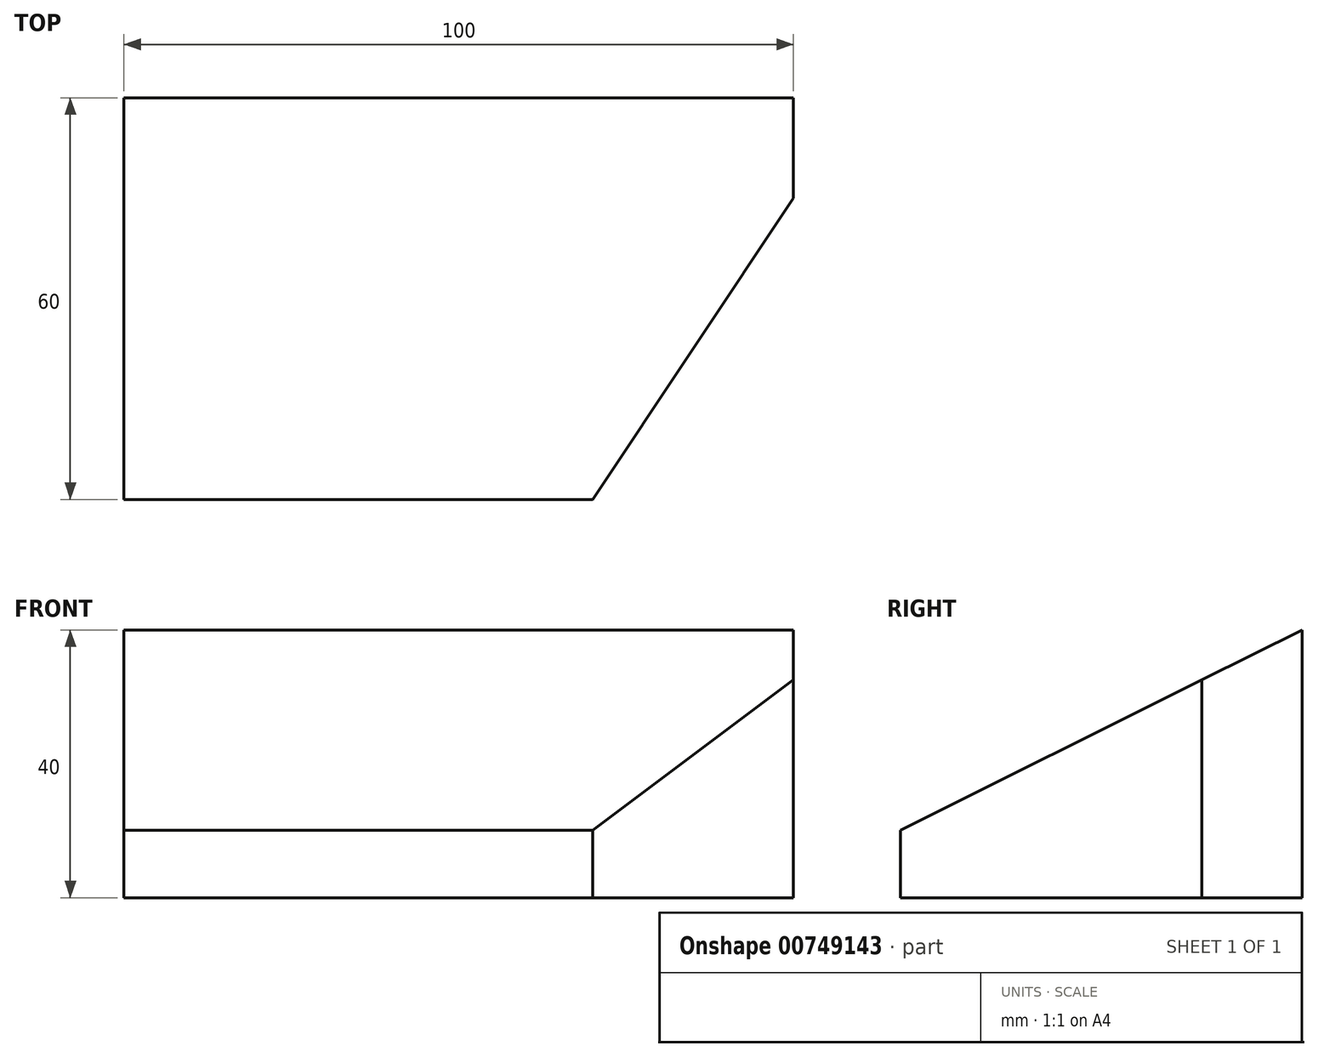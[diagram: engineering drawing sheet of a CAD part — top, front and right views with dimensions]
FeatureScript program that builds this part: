
annotation { "Feature Type Name" : "Feature", "Feature Type Description" : "" }
export const myFeature = defineFeature(function(context is Context, id is Id, definition is map)
    precondition{}
    {
        {
            var Q0;
            Q0=qCreatedBy(makeId("Top.planeOp"),FACE);
            var sketch = newSketch(context, id + "F0", { "sketchPlane" : qUnion([Q0])});
            skLineSegment(sketch, "E0", {"start": v(0, 0) * mm, "end": v(0, 60) * mm});
            skLineSegment(sketch, "E1", {"start": v(0, 60) * mm, "end": v(100, 60) * mm});
            skLineSegment(sketch, "E2", {"start": v(100, 60) * mm, "end": v(100, 45) * mm});
            skLineSegment(sketch, "E3", {"start": v(100, 45) * mm, "end": v(70, 0) * mm});
            skLineSegment(sketch, "E4", {"start": v(70, 0) * mm, "end": v(0, 0) * mm});
            skSolve(sketch);
        }
        {
            var Q0;
            Q0=makeQuery(id+"F0.imprint","IMPRINT",FACE,{"disambiguationData":[TD([[makeQuery(id+"F0.imprint","IMPRINT",EDGE,{"derivedFrom":sQuery(id+"F0.wireOp",EDGE,"E0")}),-1.0]])]});
            extrude(context, id + "F1", {"entities" : qUnion([Q0]), "depth" : 40 * mm, "offsetDistance" : 25 * mm});
        }
        {
            var Q0;
            Q0=makeQuery(id+"F1.opExtrude","SWEPT_FACE",FACE,{"disambiguationData":[OSD([sQuery(id+"F0.wireOp",EDGE,"E0")])]});
            var sketch = newSketch(context, id + "F2", { "sketchPlane" : qUnion([Q0])});
            skLineSegment(sketch, "E5", {"start": v(-60, 40) * mm, "end": v(0, 10.1) * mm});
            skSolve(sketch);
        }
        {
            var Q0;
            {var subQ0=sQuery(id+"F2.wireOp",EDGE,"E5");Q0=makeQuery(id+"F2.imprint","IMPRINT",FACE,{"disambiguationData":[TD([[makeQuery(id+"F2.imprint","IMPRINT",EDGE,{"derivedFrom":subQ0}),1.0]])]});}
            extrude(context, id + "F3", {"entities" : qUnion([Q0]), "operationType" : NewBodyOperationType.REMOVE, "oppositeDirection" : true, "depth" : 101.2 * mm, "offsetDistance" : 25 * mm});
        }
    });
